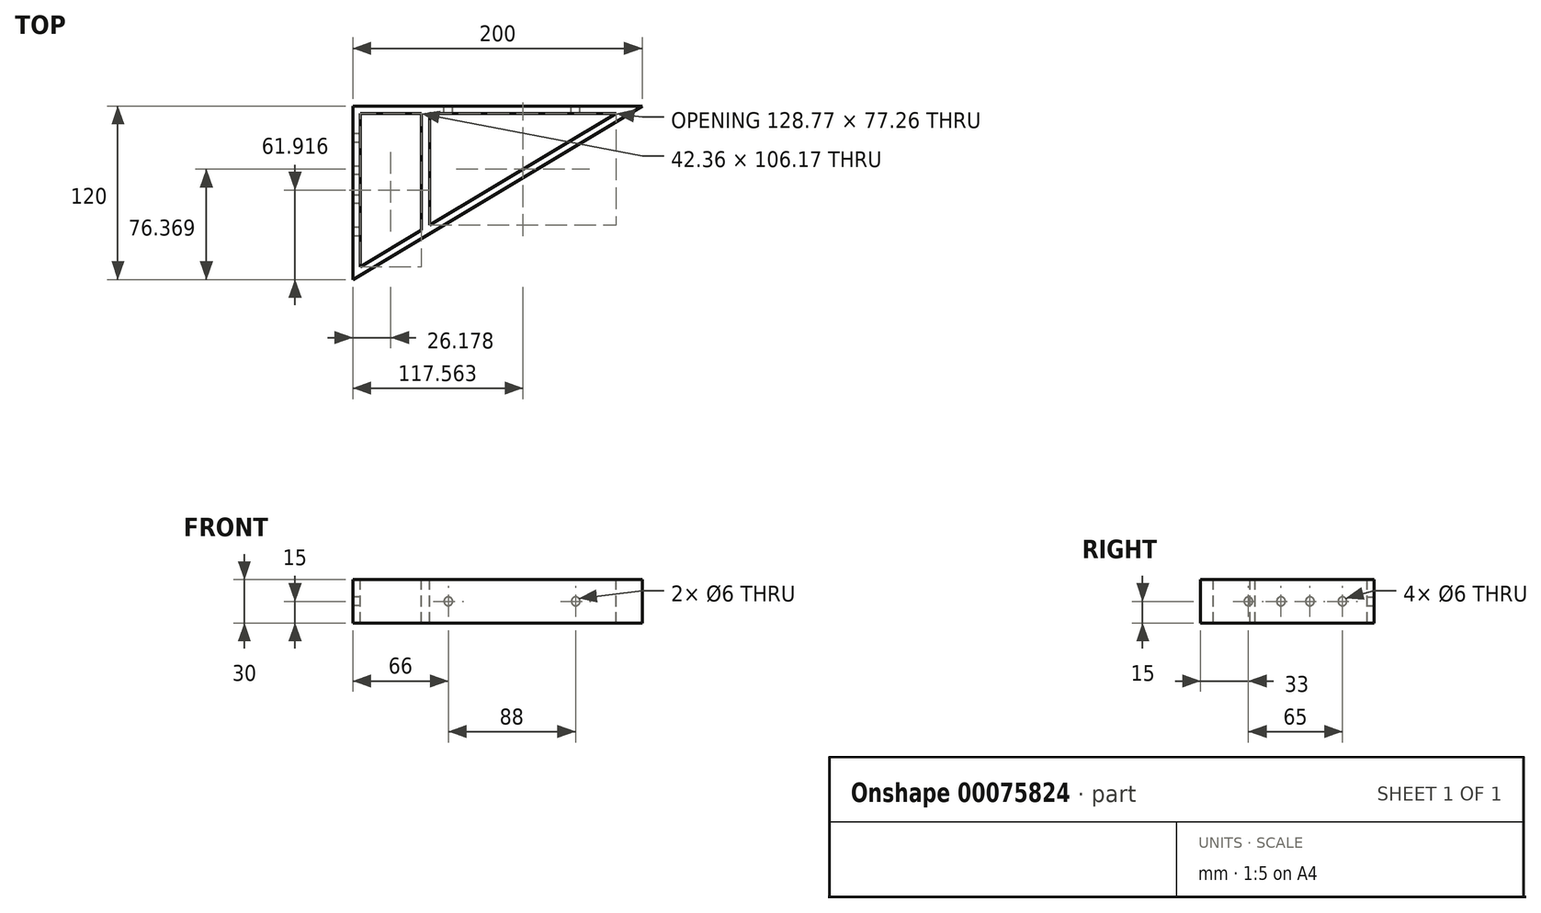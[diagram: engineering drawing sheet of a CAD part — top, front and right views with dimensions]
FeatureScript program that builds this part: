
annotation { "Feature Type Name" : "Feature", "Feature Type Description" : "" }
export const myFeature = defineFeature(function(context is Context, id is Id, definition is map)
    precondition{}
    {
        {
            var Q0;
            Q0=qCreatedBy(makeId("Top.planeOp"),FACE);
            var sketch = newSketch(context, id + "F0", { "sketchPlane" : qUnion([Q0])});
            skLineSegment(sketch, "E0.bottom", {"start": v(0, 0) * mm, "end": v(-200, 0) * mm});
            skLineSegment(sketch, "E0.top", {"start": v(0, 120) * mm, "end": v(-200, 120) * mm});
            skLineSegment(sketch, "E0.left", {"start": v(0, 0) * mm, "end": v(0, 120) * mm});
            skLineSegment(sketch, "E0.right", {"start": v(-200, 0) * mm, "end": v(-200, 120) * mm});
            skSolve(sketch);
        }
        {
            var Q0;
            Q0=makeQuery(id+"F0.imprint","IMPRINT",FACE,{"disambiguationData":[TD([[makeQuery(id+"F0.imprint","IMPRINT",EDGE,{"derivedFrom":sQuery(id+"F0.wireOp",EDGE,"E0.bottom")}),-1.0]])]});
            extrude(context, id + "F1", {"entities" : qUnion([Q0]), "depth" : 30 * mm});
        }
        {
            var Q0;
            Q0=makeQuery(id+"F1.opExtrude","CAP_FACE",FACE,{"disambiguationData":[OSD([sQuery(id+"F0.wireOp",EDGE,"E0.bottom"),sQuery(id+"F0.wireOp",EDGE,"E0.top"),sQuery(id+"F0.wireOp",EDGE,"E0.left"),sQuery(id+"F0.wireOp",EDGE,"E0.right")])],"isStart":false});
            var sketch = newSketch(context, id + "F2", { "sketchPlane" : qUnion([Q0])});
            skLineSegment(sketch, "E1", {"start": v(-200, 0) * mm, "end": v(0, 120) * mm});
            skSolve(sketch);
        }
        {
            var Q0;
            Q0=makeQuery(id+"F2.imprint","IMPRINT",FACE,{"disambiguationData":[TD([[makeQuery(id+"F2.imprint","IMPRINT",EDGE,{"derivedFrom":sQuery(id+"F2.wireOp",EDGE,"E1")}),-1.0]])]});
            extrude(context, id + "F3", {"entities" : qUnion([Q0]), "operationType" : NewBodyOperationType.REMOVE, "oppositeDirection" : true, "depth" : 30 * mm});
        }
        {
            var Q0;
            Q0=makeQuery(id+"F1.opExtrude","CAP_FACE",FACE,{"disambiguationData":[OSD([sQuery(id+"F0.wireOp",EDGE,"E0.bottom"),sQuery(id+"F0.wireOp",EDGE,"E0.top"),sQuery(id+"F0.wireOp",EDGE,"E0.left"),sQuery(id+"F0.wireOp",EDGE,"E0.right")])],"isStart":false});
            var sketch = newSketch(context, id + "F4", { "sketchPlane" : qUnion([Q0])});
            skLineSegment(sketch, "E2", {"start": v(-195, 8.83) * mm, "end": v(-195, 115) * mm});
            skLineSegment(sketch, "E3", {"start": v(-195, 115) * mm, "end": v(-18.05, 115) * mm});
            skLineSegment(sketch, "E4", {"start": v(-18.05, 115) * mm, "end": v(-195, 8.83) * mm});
            skLineSegment(sketch, "E5", {"start": v(-115.8, 115) * mm, "end": v(-115.8, 120) * mm});
            skLineSegment(sketch, "E6", {"start": v(-111.47, 58.95) * mm, "end": v(-108.9, 54.66) * mm});
            skLineSegment(sketch, "E7", {"start": v(-195, 60.92) * mm, "end": v(-200, 60.92) * mm});
            skLineSegment(sketch, "E8", {"start": v(-146.82, 115) * mm, "end": v(-146.82, 37.74) * mm});
            skLineSegment(sketch, "E9", {"start": v(-146.82, 37.74) * mm, "end": v(-152.64, 34.24) * mm});
            skLineSegment(sketch, "E10", {"start": v(-152.64, 34.24) * mm, "end": v(-152.64, 115) * mm});
            skLineSegment(sketch, "E11", {"start": v(-152.64, 115) * mm, "end": v(-146.82, 115) * mm});
            skSolve(sketch);
        }
        {
            var Q0;
            {var subQ0=sQuery(id+"F4.wireOp",EDGE,"E4");var subQ4=sQuery(id+"F4.wireOp",EDGE,"E2");var subQ8=makeQuery(id+"F4.imprint","INTERSECT",VERTEX,{"derivedFrom":[subQ4,subQ0]});Q0=makeQuery(id+"F4.imprint","IMPRINT",FACE,{"disambiguationData":[TD([[makeQuery(id+"F4.imprint","IMPRINT",EDGE,{"disambiguationData":[TD([[subQ8,-1.0]])],"derivedFrom":subQ4}),-1.0]])]});}
            var Q1;
            {var subQ2=sQuery(id+"F4.wireOp",EDGE,"E8");Q1=makeQuery(id+"F4.imprint","IMPRINT",FACE,{"disambiguationData":[TD([[makeQuery(id+"F4.imprint","IMPRINT",EDGE,{"derivedFrom":subQ2}),1.0]])]});}
            extrude(context, id + "F5", {"entities" : qUnion([Q0, Q1]), "operationType" : NewBodyOperationType.REMOVE, "oppositeDirection" : true, "depth" : 30 * mm});
        }
        {
            var Q0;
            Q0=makeQuery(id+"F1.opExtrude","SWEPT_FACE",FACE,{"disambiguationData":[OSD([sQuery(id+"F0.wireOp",EDGE,"E0.top")])]});
            var sketch = newSketch(context, id + "F6", { "sketchPlane" : qUnion([Q0])});
            skPoint(sketch, "E12", {"position": v(0, 15) * mm});
            skPoint(sketch, "E13", {"position": v(200, 15) * mm});
            skLineSegment(sketch, "E14", {"start": v(0, 15) * mm, "end": v(46, 15) * mm});
            skLineSegment(sketch, "E15", {"start": v(46, 15) * mm, "end": v(134, 15) * mm});
            skCircle(sketch, "E16", {"center": v(46, 15) * mm, "radius": 3 * mm});
            skCircle(sketch, "E17", {"center": v(134, 15) * mm, "radius": 3 * mm});
            skSolve(sketch);
        }
        {
            var Q0;
            Q0=makeQuery(id+"F6.imprint","IMPRINT",FACE,{"disambiguationData":[TD([[makeQuery(id+"F6.imprint","IMPRINT",EDGE,{"derivedFrom":sQuery(id+"F6.wireOp",EDGE,"E17")}),1.0]])]});
            var Q1;
            {var subQ0=sQuery(id+"F6.wireOp",EDGE,"E15");var subQ1=sQuery(id+"F6.wireOp",EDGE,"E14");var subQ2=makeQuery(id+"F6.imprint","INTERSECT",VERTEX,{"derivedFrom":[subQ1,subQ0]});Q1=makeQuery(id+"F6.imprint","IMPRINT",FACE,{"disambiguationData":[TD([[makeQuery(id+"F6.imprint","IMPRINT",EDGE,{"disambiguationData":[TD([[subQ2,1.0]])],"derivedFrom":subQ1}),-1.0]])]});}
            var Q2;
            {var subQ0=sQuery(id+"F6.wireOp",EDGE,"E15");var subQ1=sQuery(id+"F6.wireOp",EDGE,"E14");var subQ2=makeQuery(id+"F6.imprint","INTERSECT",VERTEX,{"derivedFrom":[subQ1,subQ0]});Q2=makeQuery(id+"F6.imprint","IMPRINT",FACE,{"disambiguationData":[TD([[makeQuery(id+"F6.imprint","IMPRINT",EDGE,{"disambiguationData":[TD([[subQ2,1.0]])],"derivedFrom":subQ1}),1.0]])]});}
            extrude(context, id + "F7", {"entities" : qUnion([Q0, Q1, Q2]), "operationType" : NewBodyOperationType.REMOVE, "oppositeDirection" : true, "depth" : 6 * mm});
        }
        {
            var Q0;
            Q0=makeQuery(id+"F1.opExtrude","SWEPT_FACE",FACE,{"disambiguationData":[OSD([sQuery(id+"F0.wireOp",EDGE,"E0.right")])]});
            var sketch = newSketch(context, id + "F8", { "sketchPlane" : qUnion([Q0])});
            skPoint(sketch, "E18", {"position": v(0, 15) * mm});
            skPoint(sketch, "E19", {"position": v(-120, 15) * mm});
            skLineSegment(sketch, "E20", {"start": v(0, 15) * mm, "end": v(-33, 15) * mm});
            skLineSegment(sketch, "E21", {"start": v(-33, 15) * mm, "end": v(-55.5, 15) * mm});
            skLineSegment(sketch, "E22", {"start": v(-55.5, 15) * mm, "end": v(-75.5, 15) * mm});
            skLineSegment(sketch, "E23", {"start": v(-75.5, 15) * mm, "end": v(-98, 15) * mm});
            skLineSegment(sketch, "E24", {"start": v(-98, 15) * mm, "end": v(-120, 15) * mm});
            skCircle(sketch, "E25", {"center": v(-33, 15) * mm, "radius": 3 * mm});
            skCircle(sketch, "E26", {"center": v(-55.5, 15) * mm, "radius": 3 * mm});
            skCircle(sketch, "E27", {"center": v(-75.5, 15) * mm, "radius": 3 * mm});
            skCircle(sketch, "E28", {"center": v(-98, 15) * mm, "radius": 3 * mm});
            skSolve(sketch);
        }
        {
            var Q0;
            {var subQ0=sQuery(id+"F8.wireOp",EDGE,"E21");var subQ1=sQuery(id+"F8.wireOp",EDGE,"E20");var subQ2=makeQuery(id+"F8.imprint","INTERSECT",VERTEX,{"derivedFrom":[subQ1,subQ0]});Q0=makeQuery(id+"F8.imprint","IMPRINT",FACE,{"disambiguationData":[TD([[makeQuery(id+"F8.imprint","IMPRINT",EDGE,{"disambiguationData":[TD([[subQ2,1.0]])],"derivedFrom":subQ1}),-1.0]])]});}
            var Q1;
            {var subQ0=sQuery(id+"F8.wireOp",EDGE,"E21");var subQ1=sQuery(id+"F8.wireOp",EDGE,"E20");var subQ2=makeQuery(id+"F8.imprint","INTERSECT",VERTEX,{"derivedFrom":[subQ1,subQ0]});Q1=makeQuery(id+"F8.imprint","IMPRINT",FACE,{"disambiguationData":[TD([[makeQuery(id+"F8.imprint","IMPRINT",EDGE,{"disambiguationData":[TD([[subQ2,1.0]])],"derivedFrom":subQ1}),1.0]])]});}
            var Q2;
            {var subQ0=sQuery(id+"F8.wireOp",EDGE,"E22");var subQ1=sQuery(id+"F8.wireOp",EDGE,"E21");var subQ2=makeQuery(id+"F8.imprint","INTERSECT",VERTEX,{"derivedFrom":[subQ1,subQ0]});Q2=makeQuery(id+"F8.imprint","IMPRINT",FACE,{"disambiguationData":[TD([[makeQuery(id+"F8.imprint","IMPRINT",EDGE,{"disambiguationData":[TD([[subQ2,1.0]])],"derivedFrom":subQ1}),-1.0]])]});}
            var Q3;
            {var subQ0=sQuery(id+"F8.wireOp",EDGE,"E22");var subQ1=sQuery(id+"F8.wireOp",EDGE,"E21");var subQ2=makeQuery(id+"F8.imprint","INTERSECT",VERTEX,{"derivedFrom":[subQ1,subQ0]});Q3=makeQuery(id+"F8.imprint","IMPRINT",FACE,{"disambiguationData":[TD([[makeQuery(id+"F8.imprint","IMPRINT",EDGE,{"disambiguationData":[TD([[subQ2,1.0]])],"derivedFrom":subQ1}),1.0]])]});}
            var Q4;
            {var subQ0=sQuery(id+"F8.wireOp",EDGE,"E23");var subQ1=sQuery(id+"F8.wireOp",EDGE,"E22");var subQ2=makeQuery(id+"F8.imprint","INTERSECT",VERTEX,{"derivedFrom":[subQ1,subQ0]});Q4=makeQuery(id+"F8.imprint","IMPRINT",FACE,{"disambiguationData":[TD([[makeQuery(id+"F8.imprint","IMPRINT",EDGE,{"disambiguationData":[TD([[subQ2,1.0]])],"derivedFrom":subQ1}),-1.0]])]});}
            var Q5;
            {var subQ0=sQuery(id+"F8.wireOp",EDGE,"E23");var subQ1=sQuery(id+"F8.wireOp",EDGE,"E22");var subQ2=makeQuery(id+"F8.imprint","INTERSECT",VERTEX,{"derivedFrom":[subQ1,subQ0]});Q5=makeQuery(id+"F8.imprint","IMPRINT",FACE,{"disambiguationData":[TD([[makeQuery(id+"F8.imprint","IMPRINT",EDGE,{"disambiguationData":[TD([[subQ2,1.0]])],"derivedFrom":subQ1}),1.0]])]});}
            var Q6;
            {var subQ0=sQuery(id+"F8.wireOp",EDGE,"E24");var subQ1=sQuery(id+"F8.wireOp",EDGE,"E23");var subQ2=makeQuery(id+"F8.imprint","INTERSECT",VERTEX,{"derivedFrom":[subQ1,subQ0]});Q6=makeQuery(id+"F8.imprint","IMPRINT",FACE,{"disambiguationData":[TD([[makeQuery(id+"F8.imprint","IMPRINT",EDGE,{"disambiguationData":[TD([[subQ2,1.0]])],"derivedFrom":subQ1}),-1.0]])]});}
            var Q7;
            {var subQ0=sQuery(id+"F8.wireOp",EDGE,"E24");var subQ1=sQuery(id+"F8.wireOp",EDGE,"E23");var subQ2=makeQuery(id+"F8.imprint","INTERSECT",VERTEX,{"derivedFrom":[subQ1,subQ0]});Q7=makeQuery(id+"F8.imprint","IMPRINT",FACE,{"disambiguationData":[TD([[makeQuery(id+"F8.imprint","IMPRINT",EDGE,{"disambiguationData":[TD([[subQ2,1.0]])],"derivedFrom":subQ1}),1.0]])]});}
            extrude(context, id + "F9", {"entities" : qUnion([Q0, Q1, Q2, Q3, Q4, Q5, Q6, Q7]), "operationType" : NewBodyOperationType.REMOVE, "oppositeDirection" : true, "depth" : 6 * mm});
        }
    });
